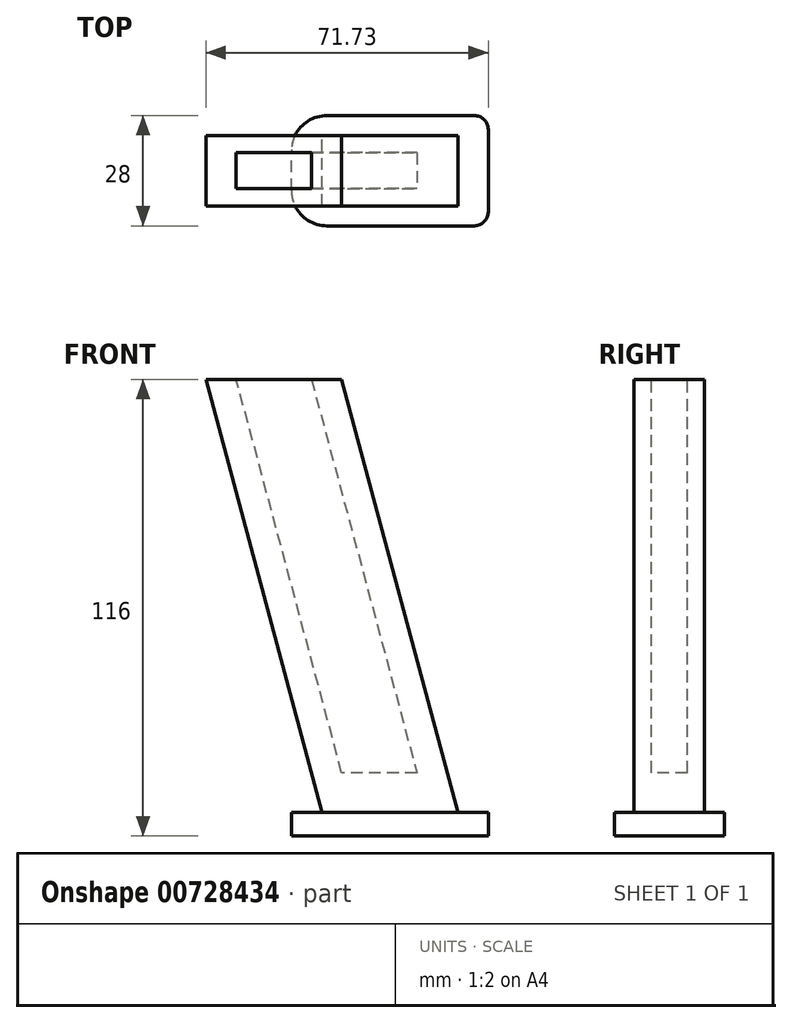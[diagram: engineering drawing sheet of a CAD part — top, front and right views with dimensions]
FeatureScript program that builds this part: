
annotation { "Feature Type Name" : "Feature", "Feature Type Description" : "" }
export const myFeature = defineFeature(function(context is Context, id is Id, definition is map)
    precondition{}
    {
        {
            var Q0;
            Q0=qCreatedBy(makeId("Front.planeOp"),FACE);
            var sketch = newSketch(context, id + "F0", { "sketchPlane" : qUnion([Q0])});
            skLineSegment(sketch, "E0", {"start": v(-13.96, 50.52) * mm, "end": v(20.54, 50.52) * mm});
            skLineSegment(sketch, "E1", {"start": v(20.54, 50.52) * mm, "end": v(50.02, -59.48) * mm});
            skLineSegment(sketch, "E2", {"start": v(-13.96, 50.52) * mm, "end": v(15.52, -59.48) * mm});
            skLineSegment(sketch, "E3", {"start": v(15.52, -59.48) * mm, "end": v(50.02, -59.48) * mm});
            skSolve(sketch);
        }
        {
            var Q0;
            Q0=makeQuery(id+"F0.imprint","IMPRINT",FACE,{"disambiguationData":[TD([[makeQuery(id+"F0.imprint","IMPRINT",EDGE,{"derivedFrom":sQuery(id+"F0.wireOp",EDGE,"E0")}),-1.0]])]});
            extrude(context, id + "F1", {"entities" : qUnion([Q0]), "endBound" : BoundingType.SYMMETRIC, "depth" : 17.9 * mm, "offsetDistance" : 25 * mm});
        }
        {
            var Q0;
            Q0=makeQuery(id+"F1.opExtrude","SWEPT_FACE",FACE,{"disambiguationData":[OSD([sQuery(id+"F0.wireOp",EDGE,"E3")])]});
            var sketch = newSketch(context, id + "F2", { "sketchPlane" : qUnion([Q0])});
            skLineSegment(sketch, "E4.bottom", {"start": v(7.77, 14) * mm, "end": v(57.77, 14) * mm});
            skLineSegment(sketch, "E4.top", {"start": v(7.77, -14) * mm, "end": v(57.77, -14) * mm});
            skLineSegment(sketch, "E4.left", {"start": v(7.77, 14) * mm, "end": v(7.77, -14) * mm});
            skLineSegment(sketch, "E4.right", {"start": v(57.77, 14) * mm, "end": v(57.77, -14) * mm});
            skSolve(sketch);
        }
        {
            var Q0;
            Q0=makeQuery(id+"F2.imprint","IMPRINT",FACE,{"disambiguationData":[TD([[makeQuery(id+"F2.imprint","IMPRINT",EDGE,{"derivedFrom":sQuery(id+"F2.wireOp",EDGE,"E4.bottom")}),-1.0]])]});
            var Q1;
            {var subQ0=sQuery(id+"F0.wireOp",EDGE,"E3");Q1=makeQuery(id+"F2.imprint","IMPRINT",FACE,{"disambiguationData":[TD([[makeQuery(id+"F2.imprint","IMPRINT",EDGE,{"derivedFrom":makeQuery(id+"F1.opExtrude","CAP_EDGE",EDGE,{"disambiguationData":[OSD([subQ0])],"isStart":true})}),1.0]])]});}
            extrude(context, id + "F3", {"entities" : qUnion([Q0, Q1]), "operationType" : NewBodyOperationType.ADD, "depth" : 6 * mm, "offsetDistance" : 25 * mm});
        }
        {
            var Q0;
            Q0=qCreatedBy(makeId("Front.planeOp"),FACE);
            var sketch = newSketch(context, id + "F4", { "sketchPlane" : qUnion([Q0])});
            skLineSegment(sketch, "E5", {"start": v(-6.26, 50.52) * mm, "end": v(12.84, 50.52) * mm});
            skLineSegment(sketch, "E6", {"start": v(12.84, 50.52) * mm, "end": v(39.64, -49.48) * mm});
            skLineSegment(sketch, "E7", {"start": v(39.64, -49.48) * mm, "end": v(20.54, -49.48) * mm});
            skLineSegment(sketch, "E8", {"start": v(20.54, -49.48) * mm, "end": v(-6.26, 50.52) * mm});
            skSolve(sketch);
        }
        {
            var Q0;
            Q0=makeQuery(id+"F4.imprint","IMPRINT",FACE,{"disambiguationData":[TD([[makeQuery(id+"F4.imprint","IMPRINT",EDGE,{"derivedFrom":sQuery(id+"F4.wireOp",EDGE,"E5")}),-1.0]])]});
            extrude(context, id + "F5", {"entities" : qUnion([Q0]), "operationType" : NewBodyOperationType.REMOVE, "endBound" : BoundingType.SYMMETRIC, "oppositeDirection" : true, "depth" : 9.1 * mm, "offsetDistance" : 25 * mm});
        }
        {
            var Q0;
            Q0=makeQuery(id+"F3.opExtrude","SWEPT_EDGE",EDGE,{"disambiguationData":[OSD([sQuery(id+"F2.wireOp",EDGE,"E4.bottom"),sQuery(id+"F2.wireOp",EDGE,"E4.right")])]});
            var Q1;
            Q1=makeQuery(id+"F3.opExtrude","SWEPT_EDGE",EDGE,{"disambiguationData":[OSD([sQuery(id+"F2.wireOp",EDGE,"E4.top"),sQuery(id+"F2.wireOp",EDGE,"E4.right")])]});
            fillet(context, id + "F6", {"entities" : qUnion([Q0, Q1]), "radius" : 3.5 * mm, "tangentPropagation" : true, "allowEdgeOverflow" : false});
        }
        {
            var Q0;
            Q0=makeQuery(id+"F3.opExtrude","SWEPT_EDGE",EDGE,{"disambiguationData":[OSD([sQuery(id+"F2.wireOp",EDGE,"E4.bottom"),sQuery(id+"F2.wireOp",EDGE,"E4.left")])]});
            var Q1;
            Q1=makeQuery(id+"F3.opExtrude","SWEPT_EDGE",EDGE,{"disambiguationData":[OSD([sQuery(id+"F2.wireOp",EDGE,"E4.top"),sQuery(id+"F2.wireOp",EDGE,"E4.left")])]});
            fillet(context, id + "F7", {"entities" : qUnion([Q0, Q1]), "radius" : 9 * mm, "tangentPropagation" : true, "allowEdgeOverflow" : false});
        }
    });
